# Revit family: QF_ELECTROLUXPROFESSIONAL_586114_PBOT15GWCO
name_source: partatom
category: Specialty Equipment
revit_build: Autodesk Revit 2018 (Build: 20190510_1515(x64)
units: mm (PartAtom-declared; Revit-internal decimal feet)

## family parameters
Always vertical = Yes
Cut with Voids When Loaded = No
Part Type = Normal
Room Calculation Point = No
Round Connector Dimension = Use Radius
Shared = Yes
Work Plane-Based = No

## types (1)
- 586114_GAS BOILING PAN_ELECT._TILTING_150LT_WALL MOUNT
    50 Hertz Option = No
    60 Hertz Option = Yes
    Apparent Power = 0 VA
    Base Height = 500 mm  [stored 1.64042 ft]
    Cold Water Connection Height = 395 mm  [stored 1.29593 ft]
    Cold Water Radius Size = 6 mm  [stored 0.019685 ft]
    Cold Water Size = 1"
    Conn Conduit = Yes
    Cycle = 60 Hz
    Depth = 1000 mm  [stored 3.28084 ft]
    Description = High Productivity Cooking Gas Tilting Boiling Pan-150lt-Wall Mounted
    Dim A = 500 mm  [stored 1.64042 ft]
    Dim B = 1750 mm  [stored 5.74147 ft]
    Direct Waste Size = 0"
    Elec Conn Connection Height = 450 mm  [stored 1.47638 ft]
    Electrical Remarks = 1PH+N 50/60HZ COMPATIBLE
    FL Amps = 0 A
    Gas Input = 92043.0 Btu/h
    Gas KW = 27
    Gas RI Connection Height = 345 mm  [stored 1.13189 ft]
    Gas Raduis Size = 13 mm
    Gas Size = 1"
    HP = 0.3 HP
    Height = 900 mm  [stored 2.95276 ft]
    Hot Water Connection Height = 395 mm  [stored 1.29593 ft]
    Hot Water Flow = 0 GPM
    Hot Water Radius Size = 6 mm  [stored 0.019685 ft]
    Hot Water Size = 1"
    Indirect Waste Connection Height = 0 mm  [stored 0 ft]
    Indirect Waste Radius Size = 0 mm  [stored 0 ft]
    Indirect Waste Size = 0"
    Manufacturer = ELECTROLUX
    Max Overcurrent Protection = 5 A
    Min Ckt Ampacity = 0 A
    Model = 586114
    Phase = 1
    Plumbing Remarks = For Domestic Water Connection
    URL = www.electrolux.com/foodservice
    URL Cutsheet = www.electrolux.com/foodservice
    URL Manufacturer = www.electrolux.com/foodservice
    Vessel Depth = 465 mm  [stored 1.52559 ft]
    Vessel Diameter = 710 mm
    Volts = 230 V
    Watts = 0 W
    Weight = 270 kg
    Width = 1300 mm  [stored 4.26509 ft]

note: [stored X ft] marks values corroborated as IEEE doubles in the binary element streams (Revit-internal decimal feet)

## geometry (parser evidence)
native form markers: Blend x27, Sweep x5
no freeform markers — native parametric forms only
